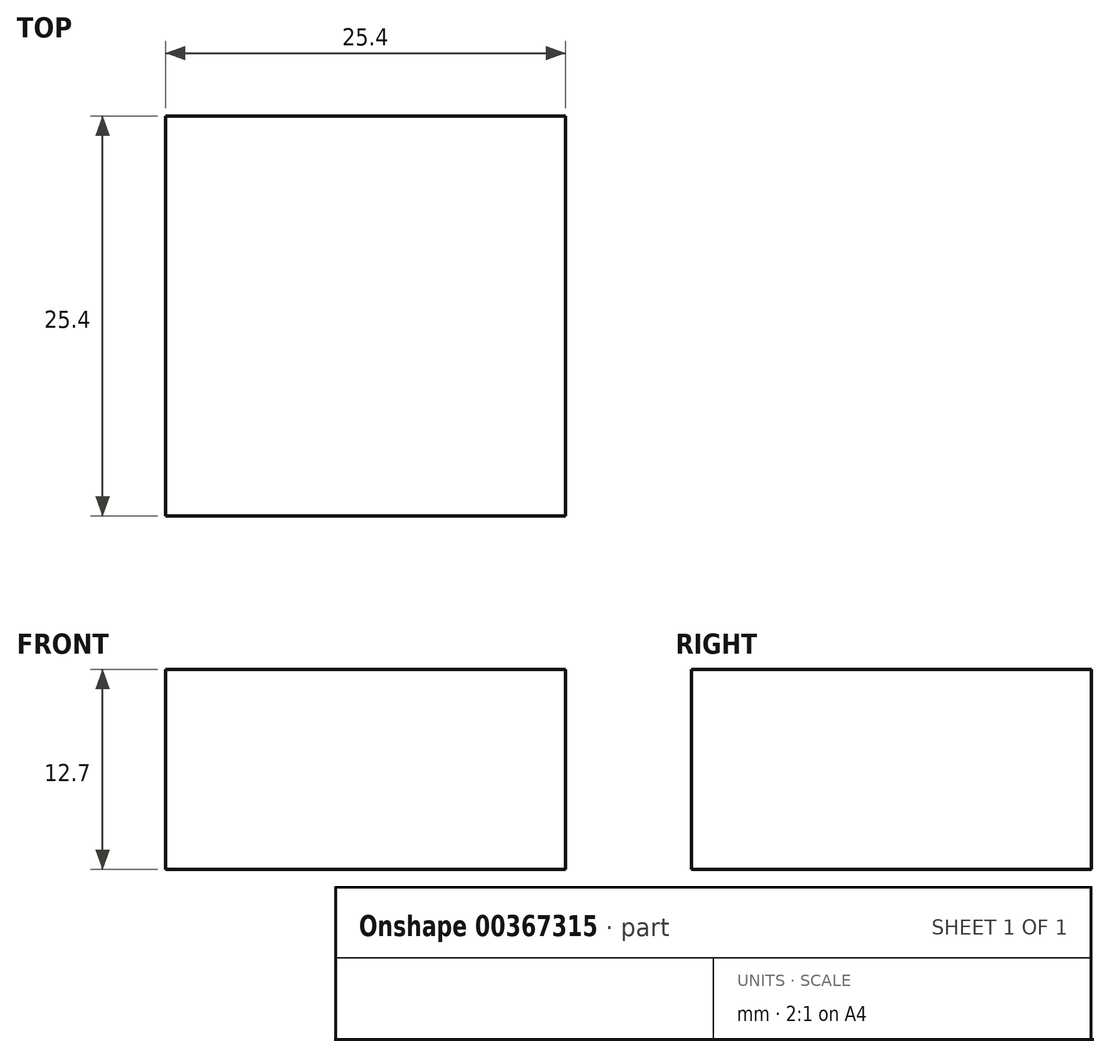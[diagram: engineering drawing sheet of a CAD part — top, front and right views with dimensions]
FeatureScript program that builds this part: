
annotation { "Feature Type Name" : "Feature", "Feature Type Description" : "" }
export const myFeature = defineFeature(function(context is Context, id is Id, definition is map)
    precondition{}
    {
        {
            var Q0;
            Q0=qCreatedBy(makeId("Top.planeOp"),FACE);
            var sketch = newSketch(context, id + "F0", { "sketchPlane" : qUnion([Q0])});
            skLineSegment(sketch, "E0.bottom", {"start": v(-12.7, 12.7) * mm, "end": v(12.7, 12.7) * mm});
            skLineSegment(sketch, "E0.top", {"start": v(-12.7, -12.7) * mm, "end": v(12.7, -12.7) * mm});
            skLineSegment(sketch, "E0.left", {"start": v(-12.7, 12.7) * mm, "end": v(-12.7, -12.7) * mm});
            skLineSegment(sketch, "E0.right", {"start": v(12.7, 12.7) * mm, "end": v(12.7, -12.7) * mm});
            skSolve(sketch);
        }
        {
            var Q0;
            Q0=makeQuery(id+"F0.imprint","IMPRINT",FACE,{"disambiguationData":[TD([[makeQuery(id+"F0.imprint","IMPRINT",EDGE,{"derivedFrom":sQuery(id+"F0.wireOp",EDGE,"E0.bottom")}),-1.0]])]});
            extrude(context, id + "F1", {"entities" : qUnion([Q0]), "depth" : 12.7 * mm});
        }
    });
